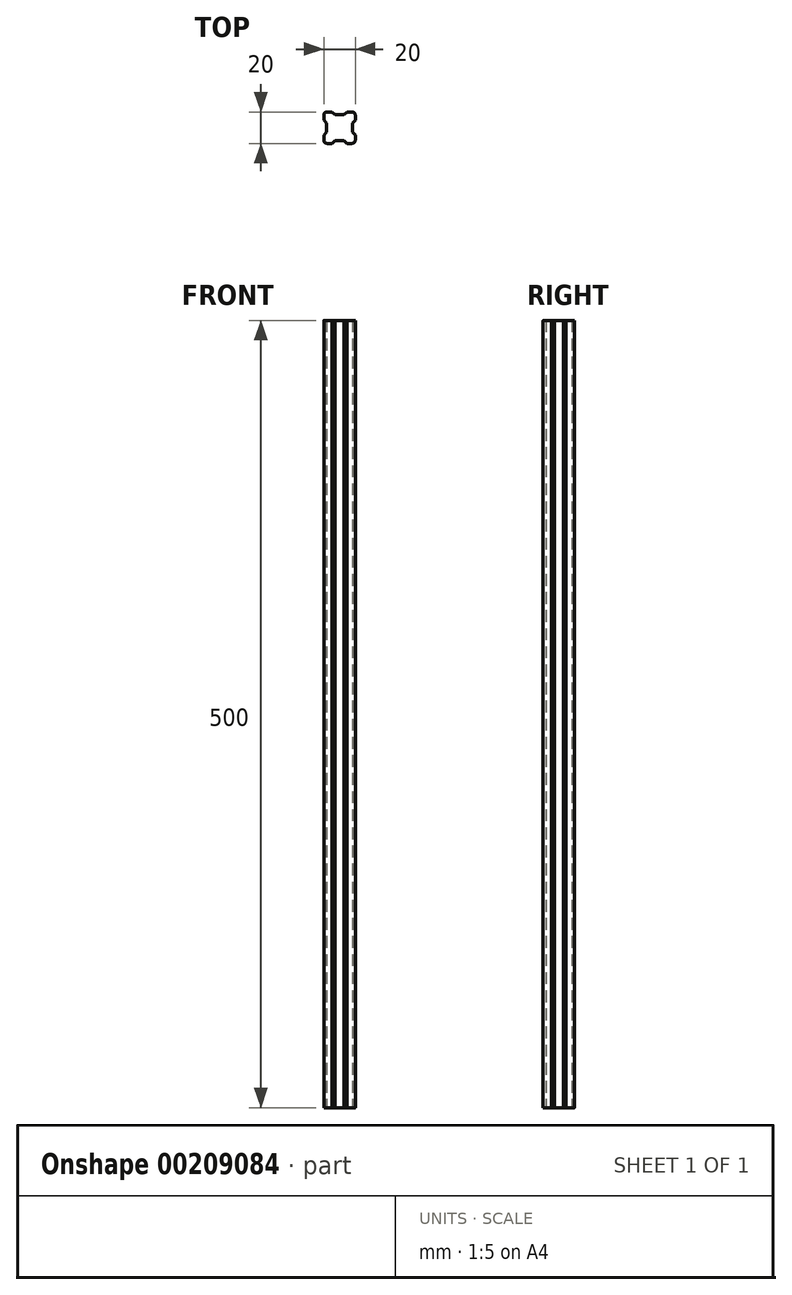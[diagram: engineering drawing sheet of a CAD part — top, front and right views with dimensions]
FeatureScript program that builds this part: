
annotation { "Feature Type Name" : "Feature", "Feature Type Description" : "" }
export const myFeature = defineFeature(function(context is Context, id is Id, definition is map)
    precondition{}
    {
        {
            var Q0;
            Q0=qCreatedBy(makeId("Top.planeOp"),FACE);
            var sketch = newSketch(context, id + "F0", { "sketchPlane" : qUnion([Q0])});
            skLineSegment(sketch, "E0.rect.bottom", {"start": v(8, 10) * mm, "end": v(-8, 10) * mm});
            skLineSegment(sketch, "E0.rect.top", {"start": v(8, -10) * mm, "end": v(-8, -10) * mm});
            skLineSegment(sketch, "E0.rect.left", {"start": v(10, 8) * mm, "end": v(10, -8) * mm});
            skLineSegment(sketch, "E0.rect.right", {"start": v(-10, 8) * mm, "end": v(-10, -8) * mm});
            skPoint(sketch, "E0.rect.middle", {"position": v(0, 0) * mm});
            skLineSegment(sketch, "E1.rect.bottom", {"start": v(-8.2, 8.2) * mm, "end": v(-2.84, 8.2) * mm, "construction": true});
            skLineSegment(sketch, "E1.rect.top", {"start": v(-8.2, -8.2) * mm, "end": v(-2.84, -8.2) * mm, "construction": true});
            skLineSegment(sketch, "E1.rect.left", {"start": v(-8.2, 8.2) * mm, "end": v(-8.2, 2.84) * mm, "construction": true});
            skLineSegment(sketch, "E1.rect.right", {"start": v(8.2, 8.2) * mm, "end": v(8.2, 2.84) * mm, "construction": true});
            skLineSegment(sketch, "E2", {"start": v(-10, 4.64) * mm, "end": v(-8.2, 2.84) * mm});
            skLineSegment(sketch, "E3", {"start": v(-8.2, -2.84) * mm, "end": v(-10, -4.64) * mm});
            skLineSegment(sketch, "E4", {"start": v(-2.84, -8.2) * mm, "end": v(-4.64, -10) * mm});
            skLineSegment(sketch, "E5", {"start": v(2.84, -8.2) * mm, "end": v(4.64, -10) * mm});
            skLineSegment(sketch, "E6", {"start": v(8.2, -2.84) * mm, "end": v(10, -4.64) * mm});
            skLineSegment(sketch, "E7", {"start": v(8.2, 2.84) * mm, "end": v(10, 4.64) * mm});
            skLineSegment(sketch, "E8", {"start": v(2.84, 8.2) * mm, "end": v(4.64, 10) * mm});
            skLineSegment(sketch, "E9", {"start": v(-2.84, 8.2) * mm, "end": v(-4.64, 10) * mm});
            skLineSegment(sketch, "E10.trimOffspring", {"start": v(-8.2, -2.84) * mm, "end": v(-8.2, -8.2) * mm, "construction": true});
            skLineSegment(sketch, "E11.trimOffspring", {"start": v(2.84, 8.2) * mm, "end": v(8.2, 8.2) * mm, "construction": true});
            skLineSegment(sketch, "E12.trimOffspring", {"start": v(8.2, -2.84) * mm, "end": v(8.2, -8.2) * mm, "construction": true});
            skLineSegment(sketch, "E13.trimOffspring", {"start": v(2.84, -8.2) * mm, "end": v(8.2, -8.2) * mm, "construction": true});
            skLineSegment(sketch, "E14", {"start": v(-8.2, 2.84) * mm, "end": v(-8.2, -2.84) * mm});
            skLineSegment(sketch, "E15", {"start": v(-2.84, 8.2) * mm, "end": v(2.84, 8.2) * mm});
            skLineSegment(sketch, "E16", {"start": v(8.2, 2.84) * mm, "end": v(8.2, -2.84) * mm});
            skLineSegment(sketch, "E17", {"start": v(2.84, -8.2) * mm, "end": v(-2.84, -8.2) * mm});
            skLineSegment(sketch, "E18", {"start": v(-8.2, 0) * mm, "end": v(0, 0) * mm, "construction": true});
            skLineSegment(sketch, "E19", {"start": v(0, 8.2) * mm, "end": v(0, 0) * mm, "construction": true});
            skLineSegment(sketch, "E20", {"start": v(8.2, 0) * mm, "end": v(0, 0) * mm, "construction": true});
            skLineSegment(sketch, "E21", {"start": v(0, -8.2) * mm, "end": v(0, 0) * mm, "construction": true});
            skPoint(sketch, "E22.visualSharp", {"position": v(-10, 10) * mm});
            skArc(sketch, "E22.filletArc", {"start": v(-8, 10) * mm, "mid": v(-9.41, 9.41) * mm, "end": v(-10, 8) * mm});
            skPoint(sketch, "E23.visualSharp", {"position": v(10, 10) * mm});
            skArc(sketch, "E23.filletArc", {"start": v(10, 8) * mm, "mid": v(9.41, 9.41) * mm, "end": v(8, 10) * mm});
            skPoint(sketch, "E24.visualSharp", {"position": v(10, -10) * mm});
            skArc(sketch, "E24.filletArc", {"start": v(8, -10) * mm, "mid": v(9.41, -9.41) * mm, "end": v(10, -8) * mm});
            skPoint(sketch, "E25.visualSharp", {"position": v(-10, -10) * mm});
            skArc(sketch, "E25.filletArc", {"start": v(-10, -8) * mm, "mid": v(-9.41, -9.41) * mm, "end": v(-8, -10) * mm});
            skSolve(sketch);
        }
        {
            var Q0;
            {var subQ8=sQuery(id+"F0.wireOp",EDGE,"E2");Q0=makeQuery(id+"F0.imprint","IMPRINT",FACE,{"disambiguationData":[TD([[makeQuery(id+"F0.imprint","IMPRINT",EDGE,{"derivedFrom":subQ8}),1.0]])]});}
            extrude(context, id + "F1", {"entities" : qUnion([Q0]), "depth" : 500 * mm});
        }
    });
